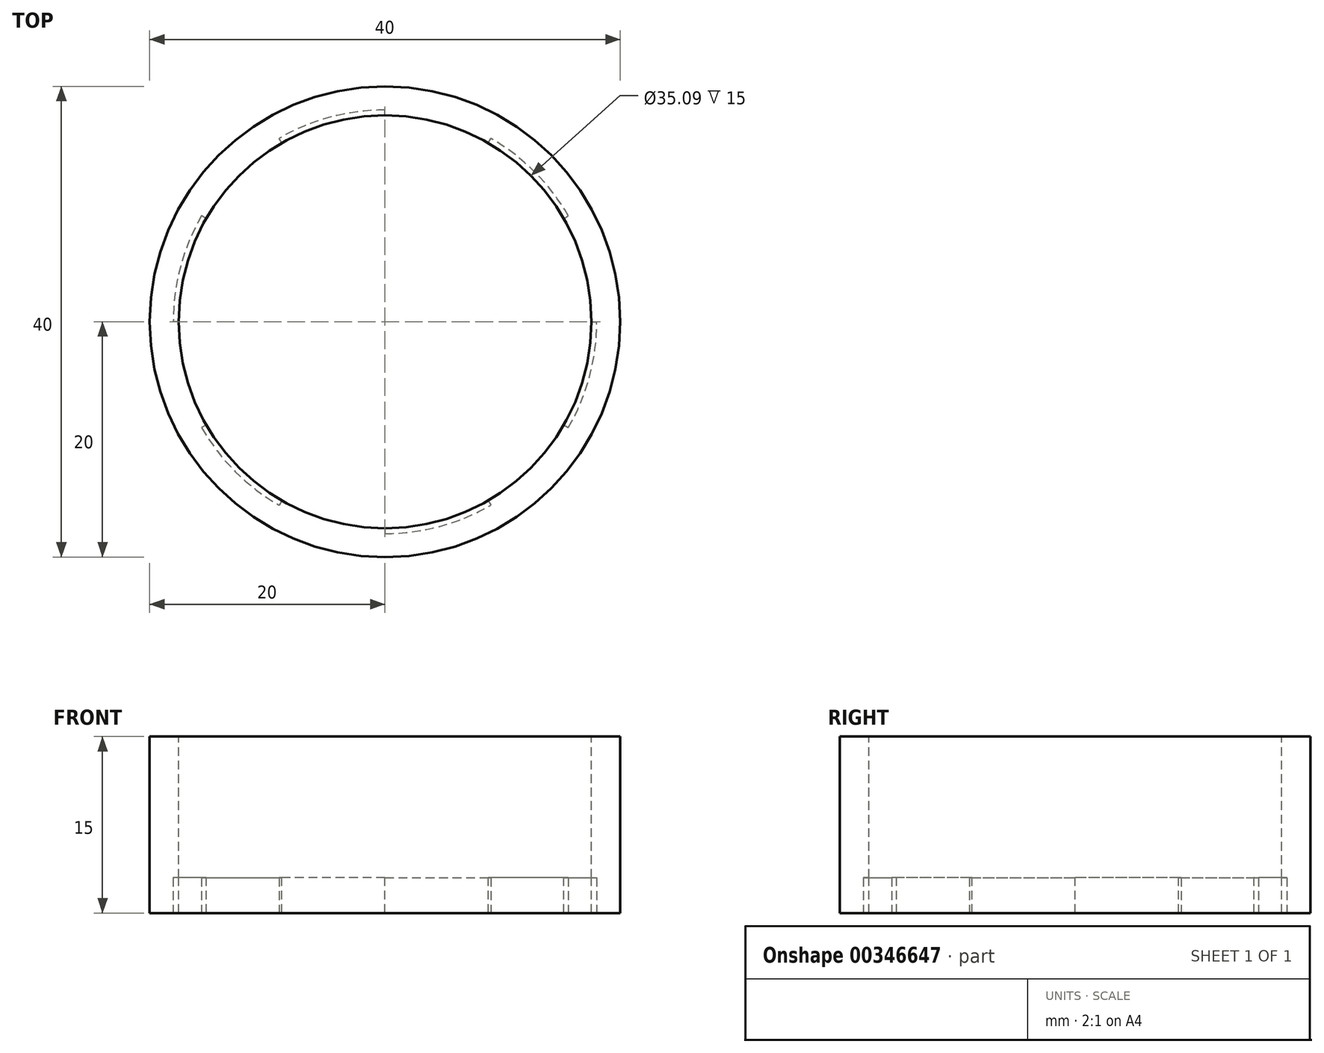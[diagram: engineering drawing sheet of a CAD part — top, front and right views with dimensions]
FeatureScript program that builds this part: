
annotation { "Feature Type Name" : "Feature", "Feature Type Description" : "" }
export const myFeature = defineFeature(function(context is Context, id is Id, definition is map)
    precondition{}
    {
        {
            var Q0;
            Q0=qCreatedBy(makeId("Top.planeOp"),FACE);
            var sketch = newSketch(context, id + "F0", { "sketchPlane" : qUnion([Q0])});
            skCircle(sketch, "E0", {"center": v(0, 0) * mm, "radius": 20 * mm});
            skSolve(sketch);
        }
        {
            var Q0;
            Q0=makeQuery(id+"F0.imprint","IMPRINT",FACE,{"disambiguationData":[TD([[makeQuery(id+"F0.imprint","IMPRINT",EDGE,{"derivedFrom":sQuery(id+"F0.wireOp",EDGE,"E0")}),1.0]])]});
            extrude(context, id + "F1", {"entities" : qUnion([Q0]), "depth" : 15 * mm});
        }
        {
            var Q0;
            Q0=makeQuery(id+"F1.opExtrude","CAP_FACE",FACE,{"disambiguationData":[OSD([sQuery(id+"F0.wireOp",EDGE,"E0")])],"isStart":false});
            var sketch = newSketch(context, id + "F2", { "sketchPlane" : qUnion([Q0])});
            skCircle(sketch, "E1", {"center": v(0, 0) * mm, "radius": 17.55 * mm});
            skSolve(sketch);
        }
        {
            var Q0;
            Q0=makeQuery(id+"F2.imprint","IMPRINT",FACE,{"disambiguationData":[TD([[makeQuery(id+"F2.imprint","IMPRINT",EDGE,{"derivedFrom":sQuery(id+"F2.wireOp",EDGE,"E1")}),1.0]])]});
            var sketch = newSketch(context, id + "F3", { "sketchPlane" : qUnion([Q0])});
            skSolve(sketch);
        }
        {
            var Q0;
            Q0 = qSketchRegion(id + "F3", true);
            var Q1;
            Q1=makeQuery(id+"F2.imprint","IMPRINT",FACE,{"disambiguationData":[TD([[makeQuery(id+"F2.imprint","IMPRINT",EDGE,{"derivedFrom":sQuery(id+"F2.wireOp",EDGE,"E1")}),1.0]])]});
            extrude(context, id + "F4", {"entities" : qUnion([Q0, Q1]), "operationType" : NewBodyOperationType.REMOVE, "oppositeDirection" : true, "depth" : 13 * mm});
        }
        {
            var Q0;
            Q0=makeQuery(id+"F0.imprint","IMPRINT",FACE,{"disambiguationData":[TD([[makeQuery(id+"F0.imprint","IMPRINT",EDGE,{"derivedFrom":sQuery(id+"F0.wireOp",EDGE,"E0")}),1.0]])]});
            var sketch = newSketch(context, id + "F5", { "sketchPlane" : qUnion([Q0])});
            skCircle(sketch, "E2", {"center": v(0, 0) * mm, "radius": 18 * mm});
            skCircle(sketch, "E3", {"center": v(0, 0) * mm, "radius": 3.5 * mm});
            skLineSegment(sketch, "E4", {"start": v(0, -3.5) * mm, "end": v(0, -18) * mm});
            skLineSegment(sketch, "E5.1.0", {"start": v(1.75, -3.03) * mm, "end": v(9, -15.59) * mm});
            skLineSegment(sketch, "E5.2.0", {"start": v(3.03, -1.75) * mm, "end": v(15.59, -9) * mm});
            skLineSegment(sketch, "E5.3.0", {"start": v(3.5, 0) * mm, "end": v(18, 0) * mm});
            skLineSegment(sketch, "E5.4.0", {"start": v(3.03, 1.75) * mm, "end": v(15.59, 9) * mm});
            skLineSegment(sketch, "E5.5.0", {"start": v(1.75, 3.03) * mm, "end": v(9, 15.59) * mm});
            skLineSegment(sketch, "E5.6.0", {"start": v(0, 3.5) * mm, "end": v(0, 18) * mm});
            skLineSegment(sketch, "E5.7.0", {"start": v(-1.75, 3.03) * mm, "end": v(-9, 15.59) * mm});
            skLineSegment(sketch, "E5.8.0", {"start": v(-3.03, 1.75) * mm, "end": v(-15.59, 9) * mm});
            skLineSegment(sketch, "E5.9.0", {"start": v(-3.5, 0) * mm, "end": v(-18, 0) * mm});
            skLineSegment(sketch, "E5.10.0", {"start": v(-3.03, -1.75) * mm, "end": v(-15.59, -9) * mm});
            skLineSegment(sketch, "E5.11.0", {"start": v(-1.75, -3.03) * mm, "end": v(-9, -15.59) * mm});
            skSolve(sketch);
        }
        {
            var Q0;
            {var subQ0=sQuery(id+"F5.wireOp",EDGE,"E4");Q0=makeQuery(id+"F5.imprint","IMPRINT",FACE,{"disambiguationData":[TD([[makeQuery(id+"F5.imprint","IMPRINT",EDGE,{"derivedFrom":subQ0}),1.0]])]});}
            var Q1;
            {var subQ0=sQuery(id+"F5.wireOp",EDGE,"E5.2.0");Q1=makeQuery(id+"F5.imprint","IMPRINT",FACE,{"disambiguationData":[TD([[makeQuery(id+"F5.imprint","IMPRINT",EDGE,{"derivedFrom":subQ0}),1.0]])]});}
            var Q2;
            {var subQ0=sQuery(id+"F5.wireOp",EDGE,"E5.4.0");Q2=makeQuery(id+"F5.imprint","IMPRINT",FACE,{"disambiguationData":[TD([[makeQuery(id+"F5.imprint","IMPRINT",EDGE,{"derivedFrom":subQ0}),1.0]])]});}
            var Q3;
            {var subQ0=sQuery(id+"F5.wireOp",EDGE,"E5.6.0");Q3=makeQuery(id+"F5.imprint","IMPRINT",FACE,{"disambiguationData":[TD([[makeQuery(id+"F5.imprint","IMPRINT",EDGE,{"derivedFrom":subQ0}),1.0]])]});}
            var Q4;
            {var subQ0=sQuery(id+"F5.wireOp",EDGE,"E5.8.0");Q4=makeQuery(id+"F5.imprint","IMPRINT",FACE,{"disambiguationData":[TD([[makeQuery(id+"F5.imprint","IMPRINT",EDGE,{"derivedFrom":subQ0}),1.0]])]});}
            var Q5;
            {var subQ0=sQuery(id+"F5.wireOp",EDGE,"E5.10.0");Q5=makeQuery(id+"F5.imprint","IMPRINT",FACE,{"disambiguationData":[TD([[makeQuery(id+"F5.imprint","IMPRINT",EDGE,{"derivedFrom":subQ0}),1.0]])]});}
            extrude(context, id + "F6", {"entities" : qUnion([Q0, Q1, Q2, Q3, Q4, Q5]), "operationType" : NewBodyOperationType.REMOVE, "depth" : 3 * mm});
        }
        {
            var Q0;
            Q0=makeQuery(id+"F2.imprint","IMPRINT",FACE,{"disambiguationData":[TD([[makeQuery(id+"F2.imprint","IMPRINT",EDGE,{"derivedFrom":sQuery(id+"F2.wireOp",EDGE,"E1")}),1.0]])]});
            extrude(context, id + "F7", {"entities" : qUnion([Q0]), "operationType" : NewBodyOperationType.REMOVE, "oppositeDirection" : true, "depth" : 25 * mm});
        }
    });
